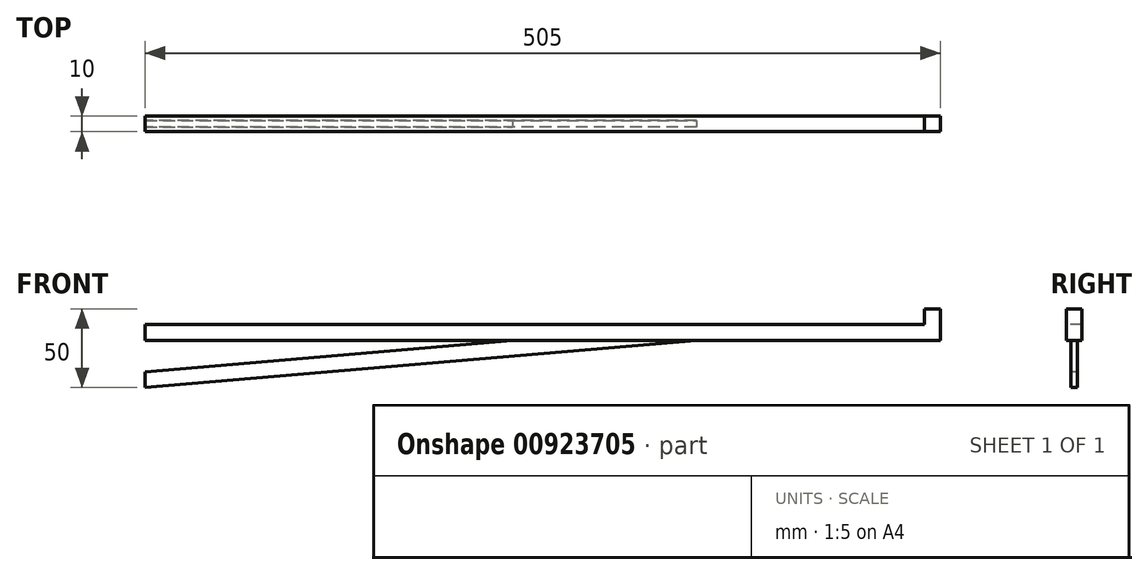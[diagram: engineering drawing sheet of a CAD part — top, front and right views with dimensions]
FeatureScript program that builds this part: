
annotation { "Feature Type Name" : "Feature", "Feature Type Description" : "" }
export const myFeature = defineFeature(function(context is Context, id is Id, definition is map)
    precondition{}
    {
        {
            var Q0;
            Q0=qCreatedBy(makeId("Top.planeOp"),FACE);
            var sketch = newSketch(context, id + "F0", { "sketchPlane" : qUnion([Q0])});
            skLineSegment(sketch, "E0.bottom", {"start": v(5, -5) * mm, "end": v(-5, -5) * mm});
            skLineSegment(sketch, "E0.top", {"start": v(5, 5) * mm, "end": v(-5, 5) * mm});
            skLineSegment(sketch, "E0.left", {"start": v(5, -5) * mm, "end": v(5, 5) * mm});
            skLineSegment(sketch, "E0.right", {"start": v(-5, -5) * mm, "end": v(-5, 5) * mm});
            skPoint(sketch, "E0.middle", {"position": v(0, 0) * mm});
            skSolve(sketch);
        }
        {
            var Q0;
            Q0=makeQuery(id+"F0.imprint","IMPRINT",FACE,{"disambiguationData":[TD([[makeQuery(id+"F0.imprint","IMPRINT",EDGE,{"derivedFrom":sQuery(id+"F0.wireOp",EDGE,"E0.bottom")}),-1.0]])]});
            extrude(context, id + "F1", {"entities" : qUnion([Q0]), "oppositeDirection" : true, "depth" : 20 * mm, "offsetDistance" : 25 * mm});
        }
        {
            var Q0;
            Q0=makeQuery(id+"F1.opExtrude","SWEPT_FACE",FACE,{"disambiguationData":[OSD([sQuery(id+"F0.wireOp",EDGE,"E0.right")])]});
            var sketch = newSketch(context, id + "F2", { "sketchPlane" : qUnion([Q0])});
            skLineSegment(sketch, "E1", {"start": v(-5, -10) * mm, "end": v(5, -10) * mm});
            skSolve(sketch);
        }
        {
            var Q0;
            Q0 = qSketchRegion(id + "F2", true);
            var Q1;
            {var subQ0=sQuery(id+"F2.wireOp",EDGE,"E1");Q1=makeQuery(id+"F2.imprint","IMPRINT",FACE,{"disambiguationData":[TD([[makeQuery(id+"F2.imprint","IMPRINT",EDGE,{"derivedFrom":subQ0}),-1.0]])]});}
            extrude(context, id + "F3", {"entities" : qUnion([Q0, Q1]), "operationType" : NewBodyOperationType.ADD, "depth" : 495 * mm, "offsetDistance" : 25 * mm});
        }
        {
            var Q0;
            {var subQ0=sQuery(id+"F0.wireOp",EDGE,"E0.right");Q0=makeQuery(id+"F3.boolean.opBoolean","MERGE",FACE,{"derivedFrom":[makeQuery(id+"F1.opExtrude","CAP_FACE",FACE,{"disambiguationData":[OSD([sQuery(id+"F0.wireOp",EDGE,"E0.bottom"),sQuery(id+"F0.wireOp",EDGE,"E0.top"),sQuery(id+"F0.wireOp",EDGE,"E0.left"),subQ0])],"isStart":false}),makeQuery(id+"F3.opExtrude","SWEPT_FACE",FACE,{"disambiguationData":[OSD([subQ0])]})]});}
            var sketch = newSketch(context, id + "F4", { "sketchPlane" : qUnion([Q0])});
            skLineSegment(sketch, "E2", {"start": v(-500, -2) * mm, "end": v(-150, -2) * mm});
            skLineSegment(sketch, "E3", {"start": v(-150, -2) * mm, "end": v(-150, 2) * mm});
            skLineSegment(sketch, "E4", {"start": v(-150, 2) * mm, "end": v(-500, 2) * mm});
            skSolve(sketch);
        }
        {
            var Q0;
            {var subQ0=sQuery(id+"F4.wireOp",EDGE,"E2");Q0=makeQuery(id+"F4.imprint","IMPRINT",FACE,{"disambiguationData":[TD([[makeQuery(id+"F4.imprint","IMPRINT",EDGE,{"derivedFrom":subQ0}),1.0]])]});}
            extrude(context, id + "F5", {"entities" : qUnion([Q0]), "operationType" : NewBodyOperationType.ADD, "depth" : 30 * mm, "offsetDistance" : 25 * mm});
        }
        {
            var Q0;
            Q0=makeQuery(id+"F5.opExtrude","SWEPT_FACE",FACE,{"disambiguationData":[OSD([sQuery(id+"F4.wireOp",EDGE,"E4")])]});
            var sketch = newSketch(context, id + "F6", { "sketchPlane" : qUnion([Q0])});
            skLineSegment(sketch, "E5", {"start": v(-150, -20) * mm, "end": v(-500, -50) * mm});
            skSolve(sketch);
        }
        {
            var Q0;
            Q0=makeQuery(id+"F6.imprint","IMPRINT",FACE,{"disambiguationData":[TD([[makeQuery(id+"F6.imprint","IMPRINT",EDGE,{"derivedFrom":sQuery(id+"F6.wireOp",EDGE,"E5")}),1.0]])]});
            extrude(context, id + "F7", {"entities" : qUnion([Q0]), "operationType" : NewBodyOperationType.REMOVE, "endBound" : BoundingType.THROUGH_ALL, "oppositeDirection" : true, "depth" : 25 * mm, "offsetDistance" : 25 * mm});
        }
        {
            var Q0;
            Q0=makeQuery(id+"F5.opExtrude","SWEPT_FACE",FACE,{"disambiguationData":[OSD([sQuery(id+"F4.wireOp",EDGE,"E4")])]});
            var sketch = newSketch(context, id + "F8", { "sketchPlane" : qUnion([Q0])});
            skLineSegment(sketch, "E6", {"start": v(-500, -40) * mm, "end": v(-266.67, -20) * mm});
            skSolve(sketch);
        }
        {
            var Q0;
            {var subQ0=sQuery(id+"F8.wireOp",EDGE,"E6");Q0=makeQuery(id+"F8.imprint","IMPRINT",FACE,{"disambiguationData":[TD([[makeQuery(id+"F8.imprint","IMPRINT",EDGE,{"derivedFrom":subQ0}),1.0]])]});}
            extrude(context, id + "F9", {"entities" : qUnion([Q0]), "operationType" : NewBodyOperationType.REMOVE, "endBound" : BoundingType.THROUGH_ALL, "oppositeDirection" : true, "depth" : 25 * mm, "offsetDistance" : 25 * mm});
        }
    });
